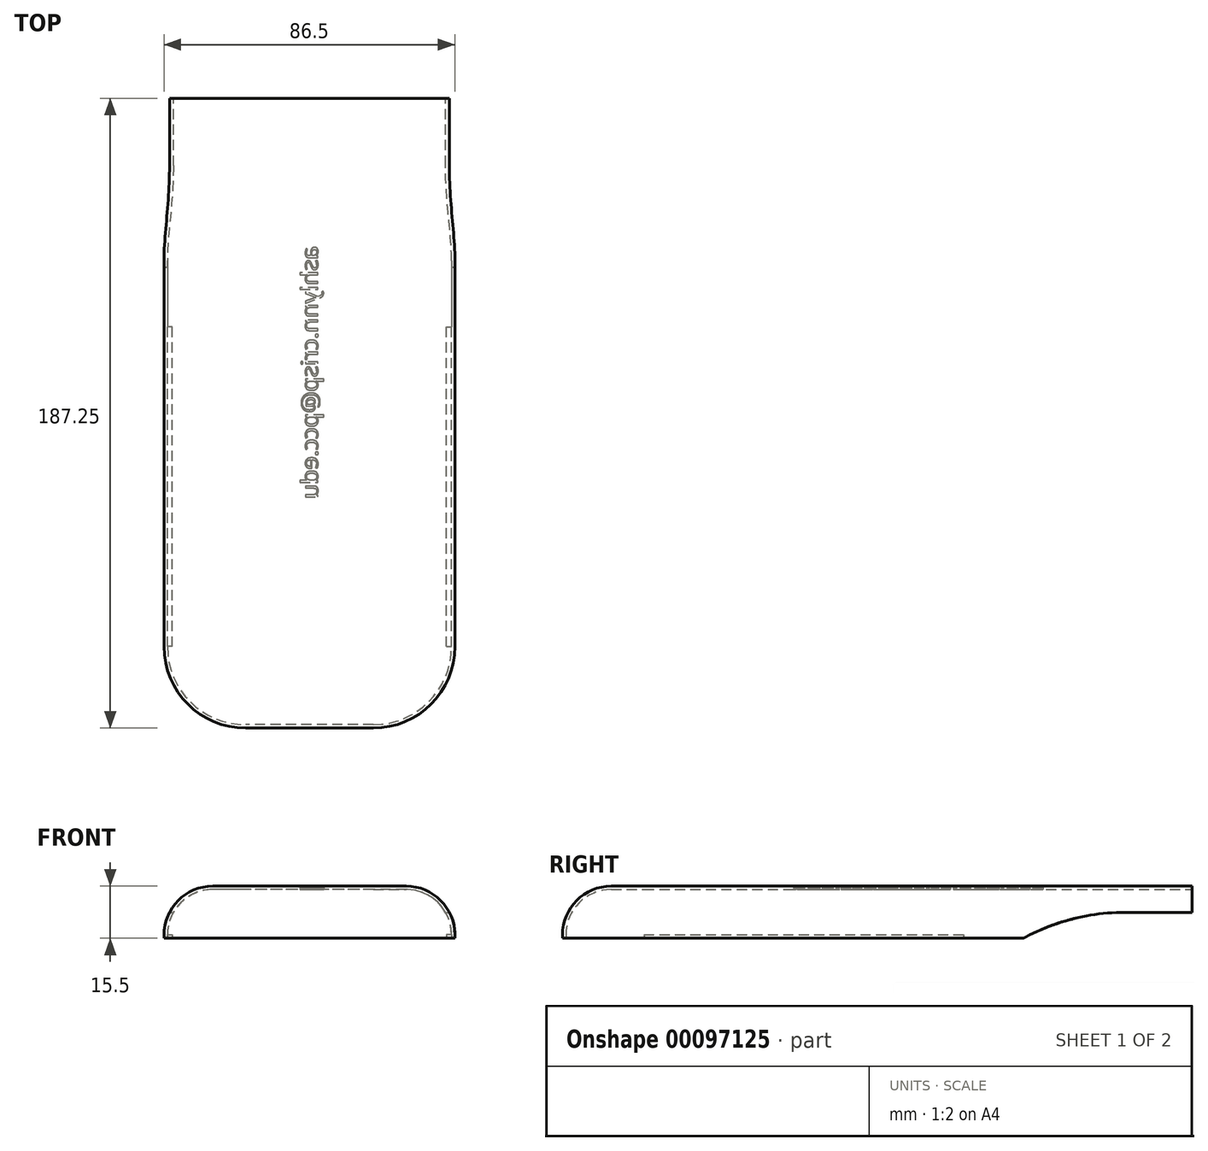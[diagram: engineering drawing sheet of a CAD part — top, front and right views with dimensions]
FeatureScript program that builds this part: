
annotation { "Feature Type Name" : "Feature", "Feature Type Description" : "" }
export const myFeature = defineFeature(function(context is Context, id is Id, definition is map)
    precondition{}
    {
        {
            var Q0;
            Q0=qCreatedBy(makeId("Front.planeOp"),FACE);
            var sketch = newSketch(context, id + "F0", { "sketchPlane" : qUnion([Q0])});
            skLineSegment(sketch, "E0", {"start": v(-28.75, 15.5) * mm, "end": v(0, 15.5) * mm});
            skLineSegment(sketch, "E1", {"start": v(0, 14.5) * mm, "end": v(-28.75, 14.5) * mm});
            skArc(sketch, "E2", {"start": v(-28.75, 15.5) * mm, "mid": v(-39, 11.25) * mm, "end": v(-43.25, 1) * mm});
            skArc(sketch, "E3", {"start": v(-28.75, 14.5) * mm, "mid": v(-38.3, 10.55) * mm, "end": v(-42.25, 1) * mm});
            skLineSegment(sketch, "E4", {"start": v(-43.25, 1) * mm, "end": v(-43.25, 0) * mm});
            skLineSegment(sketch, "E5", {"start": v(-43.25, 0) * mm, "end": v(-42.25, 0) * mm});
            skLineSegment(sketch, "E6", {"start": v(-42.25, 1) * mm, "end": v(-40.75, 1) * mm});
            skLineSegment(sketch, "E7", {"start": v(-40.75, 1) * mm, "end": v(-40.75, 0) * mm});
            skLineSegment(sketch, "E8", {"start": v(-40.75, 0) * mm, "end": v(-42.25, 0) * mm});
            skLineSegment(sketch, "E9", {"start": v(0, 15.5) * mm, "end": v(0, 14.5) * mm});
            skSolve(sketch);
        }
        {
            var Q0;
            Q0=makeQuery(id+"F0.imprint","IMPRINT",FACE,{"disambiguationData":[TD([[makeQuery(id+"F0.imprint","IMPRINT",EDGE,{"derivedFrom":sQuery(id+"F0.wireOp",EDGE,"E0")}),-1.0]])]});
            extrude(context, id + "F1", {"entities" : qUnion([Q0]), "depth" : 95 * mm});
        }
        {
            var Q0;
            Q0=makeQuery(id+"F1.opExtrude","CAP_FACE",FACE,{"disambiguationData":[OSD([sQuery(id+"F0.wireOp",EDGE,"E0"),sQuery(id+"F0.wireOp",EDGE,"E1"),sQuery(id+"F0.wireOp",EDGE,"E2"),sQuery(id+"F0.wireOp",EDGE,"E3"),sQuery(id+"F0.wireOp",EDGE,"E4"),sQuery(id+"F0.wireOp",EDGE,"E5"),sQuery(id+"F0.wireOp",EDGE,"E6"),sQuery(id+"F0.wireOp",EDGE,"E7"),sQuery(id+"F0.wireOp",EDGE,"E8"),sQuery(id+"F0.wireOp",EDGE,"a0cf0cd2-0adc-428c-8f04-1908610eca040.MirrorCS"),sQuery(id+"F0.wireOp",EDGE,"a0cf0cd2-0adc-428c-8f04-1908610eca042.MirrorCS"),sQuery(id+"F0.wireOp",EDGE,"a0cf0cd2-0adc-428c-8f04-1908610eca043.MirrorCS"),sQuery(id+"F0.wireOp",EDGE,"a0cf0cd2-0adc-428c-8f04-1908610eca044.MirrorCS"),sQuery(id+"F0.wireOp",EDGE,"a0cf0cd2-0adc-428c-8f04-1908610eca045.MirrorCS"),sQuery(id+"F0.wireOp",EDGE,"a0cf0cd2-0adc-428c-8f04-1908610eca046.MirrorCS"),sQuery(id+"F0.wireOp",EDGE,"a0cf0cd2-0adc-428c-8f04-1908610eca047.MirrorCS"),sQuery(id+"F0.wireOp",EDGE,"a0cf0cd2-0adc-428c-8f04-1908610eca048.MirrorCS"),sQuery(id+"F0.wireOp",EDGE,"e27b2194-398d-4e29-9fbd-8609b71e9a3b0.MirrorCS")])],"isStart":true});
            var sketch = newSketch(context, id + "F2", { "sketchPlane" : qUnion([Q0])});
            skLineSegment(sketch, "E10.MirrorCS", {"start": v(42.25, 1) * mm, "end": v(42.25, 0) * mm});
            skSolve(sketch);
        }
        {
            var Q0;
            {var subQ2=sQuery(id+"F2.wireOp",EDGE,"E10.MirrorCS");Q0=makeQuery(id+"F2.imprint","IMPRINT",FACE,{"disambiguationData":[TD([[makeQuery(id+"F2.imprint","IMPRINT",EDGE,{"derivedFrom":subQ2}),1.0]])]});}
            extrude(context, id + "F3", {"entities" : qUnion([Q0]), "operationType" : NewBodyOperationType.ADD, "depth" : 68 * mm});
        }
        {
            var Q0;
            Q0=makeQuery(id+"F1.opExtrude","CAP_FACE",FACE,{"disambiguationData":[OSD([sQuery(id+"F0.wireOp",EDGE,"E0"),sQuery(id+"F0.wireOp",EDGE,"E1"),sQuery(id+"F0.wireOp",EDGE,"E2"),sQuery(id+"F0.wireOp",EDGE,"E3"),sQuery(id+"F0.wireOp",EDGE,"E4"),sQuery(id+"F0.wireOp",EDGE,"E5"),sQuery(id+"F0.wireOp",EDGE,"E6"),sQuery(id+"F0.wireOp",EDGE,"E7"),sQuery(id+"F0.wireOp",EDGE,"E8"),sQuery(id+"F0.wireOp",EDGE,"a0cf0cd2-0adc-428c-8f04-1908610eca040.MirrorCS"),sQuery(id+"F0.wireOp",EDGE,"a0cf0cd2-0adc-428c-8f04-1908610eca042.MirrorCS"),sQuery(id+"F0.wireOp",EDGE,"a0cf0cd2-0adc-428c-8f04-1908610eca043.MirrorCS"),sQuery(id+"F0.wireOp",EDGE,"a0cf0cd2-0adc-428c-8f04-1908610eca044.MirrorCS"),sQuery(id+"F0.wireOp",EDGE,"a0cf0cd2-0adc-428c-8f04-1908610eca045.MirrorCS"),sQuery(id+"F0.wireOp",EDGE,"a0cf0cd2-0adc-428c-8f04-1908610eca046.MirrorCS"),sQuery(id+"F0.wireOp",EDGE,"a0cf0cd2-0adc-428c-8f04-1908610eca047.MirrorCS"),sQuery(id+"F0.wireOp",EDGE,"a0cf0cd2-0adc-428c-8f04-1908610eca048.MirrorCS"),sQuery(id+"F0.wireOp",EDGE,"e27b2194-398d-4e29-9fbd-8609b71e9a3b0.MirrorCS")])],"isStart":false});
            var sketch = newSketch(context, id + "F4", { "sketchPlane" : qUnion([Q0])});
            skLineSegment(sketch, "E11", {"start": v(-42.25, 1) * mm, "end": v(-42.25, 0) * mm});
            skLineSegment(sketch, "E12", {"start": v(-28.75, 15.5) * mm, "end": v(-28.75, 14.5) * mm});
            skLineSegment(sketch, "E13", {"start": v(-19, 15.5) * mm, "end": v(-19, 14.5) * mm});
            skSolve(sketch);
        }
        {
            var Q0;
            {var subQ0=sQuery(id+"F4.wireOp",EDGE,"E11");Q0=makeQuery(id+"F4.imprint","IMPRINT",FACE,{"disambiguationData":[TD([[makeQuery(id+"F4.imprint","IMPRINT",EDGE,{"derivedFrom":subQ0}),-1.0]])]});}
            var Q1;
            {var subQ0=sQuery(id+"F4.wireOp",EDGE,"E12");Q1=makeQuery(id+"F4.imprint","IMPRINT",FACE,{"disambiguationData":[TD([[makeQuery(id+"F4.imprint","IMPRINT",EDGE,{"derivedFrom":subQ0}),1.0]])]});}
            var Q2;
            Q2=sQuery(id+"F4.wireOp",EDGE,"E13");
            revolve(context, id + "F5", {"operationType" : NewBodyOperationType.ADD, "entities" : qUnion([Q0, Q1]), "axis" : qUnion([Q2]), "revolveType" : RevolveType.ONE_DIRECTION, "oppositeDirection" : true, "angle" : 90 * degree});
        }
        {
            var Q0;
            Q0=makeQuery(id+"F5.opRevolve","CAP_FACE",FACE,{"disambiguationData":[OSD([sQuery(id+"F0.wireOp",EDGE,"E0"),sQuery(id+"F0.wireOp",EDGE,"E1"),sQuery(id+"F0.wireOp",EDGE,"E2"),sQuery(id+"F0.wireOp",EDGE,"E3"),sQuery(id+"F0.wireOp",EDGE,"E4"),sQuery(id+"F0.wireOp",EDGE,"E5"),sQuery(id+"F0.wireOp",EDGE,"E8"),sQuery(id+"F4.wireOp",EDGE,"E11"),sQuery(id+"F4.wireOp",EDGE,"E13")])],"isStart":false});
            var sketch = newSketch(context, id + "F6", { "sketchPlane" : qUnion([Q0])});
            skLineSegment(sketch, "E14", {"start": v(-104.75, 15.5) * mm, "end": v(-104.75, 14.5) * mm});
            skSolve(sketch);
        }
        {
            var Q0;
            Q0=makeQuery(id+"F6.imprint","IMPRINT",FACE,{"disambiguationData":[TD([[makeQuery(id+"F6.imprint","IMPRINT",EDGE,{"derivedFrom":sQuery(id+"F6.wireOp",EDGE,"E14")}),1.0]])]});
            var Q1;
            {var subQ0=sQuery(id+"F0.wireOp",EDGE,"E9");Q1=makeQuery(id+"F3.boolean.opBoolean","MERGE",FACE,{"derivedFrom":[makeQuery(id+"F1.opExtrude","SWEPT_FACE",FACE,{"disambiguationData":[OSD([subQ0])]}),makeQuery(id+"F3.opExtrude","SWEPT_FACE",FACE,{"disambiguationData":[OSD([subQ0])]})]});}
            extrude(context, id + "F7", {"entities" : qUnion([Q0]), "operationType" : NewBodyOperationType.ADD, "endBound" : BoundingType.UP_TO_SURFACE, "endBoundEntityFace" : qUnion([Q1]), "depth" : 25 * mm});
        }
        {
            var Q0;
            Q0=makeQuery(id+"F5.opRevolve","CAP_FACE",FACE,{"disambiguationData":[OSD([sQuery(id+"F0.wireOp",EDGE,"E0"),sQuery(id+"F0.wireOp",EDGE,"E1"),sQuery(id+"F0.wireOp",EDGE,"E2"),sQuery(id+"F0.wireOp",EDGE,"E3"),sQuery(id+"F0.wireOp",EDGE,"E4"),sQuery(id+"F0.wireOp",EDGE,"E5"),sQuery(id+"F0.wireOp",EDGE,"E8"),sQuery(id+"F4.wireOp",EDGE,"E11"),sQuery(id+"F4.wireOp",EDGE,"E13")])],"isStart":false});
            var Q1;
            {var subQ0=sQuery(id+"F0.wireOp",EDGE,"E9");Q1=makeQuery(id+"F7.boolean.opBoolean","MERGE",FACE,{"derivedFrom":[makeQuery(id+"F3.boolean.opBoolean","MERGE",FACE,{"derivedFrom":[makeQuery(id+"F1.opExtrude","SWEPT_FACE",FACE,{"disambiguationData":[OSD([subQ0])]}),makeQuery(id+"F3.opExtrude","SWEPT_FACE",FACE,{"disambiguationData":[OSD([subQ0])]})]}),makeQuery(id+"F7.opExtrude","CAP_FACE",FACE,{"disambiguationData":[OSD([subQ0])],"isStart":false})]});}
            extrude(context, id + "F8", {"entities" : qUnion([Q0]), "operationType" : NewBodyOperationType.ADD, "endBound" : BoundingType.UP_TO_SURFACE, "endBoundEntityFace" : qUnion([Q1]), "depth" : 25 * mm});
        }
        {
            var Q0;
            Q0=makeQuery(id+"F1.opExtrude","SWEPT_BODY",BODY,{"disambiguationData":[OSD([sQuery(id+"F0.wireOp",EDGE,"E0"),sQuery(id+"F0.wireOp",EDGE,"E1"),sQuery(id+"F0.wireOp",EDGE,"E2"),sQuery(id+"F0.wireOp",EDGE,"E3"),sQuery(id+"F0.wireOp",EDGE,"E4"),sQuery(id+"F0.wireOp",EDGE,"E5"),sQuery(id+"F0.wireOp",EDGE,"E6"),sQuery(id+"F0.wireOp",EDGE,"E7"),sQuery(id+"F0.wireOp",EDGE,"E8"),sQuery(id+"F0.wireOp",EDGE,"E9")])]});
            var Q1;
            Q1=qCreatedBy(makeId("Right.planeOp"),FACE);
            mirror(context, id + "F9", {"operationType" : NewBodyOperationType.ADD, "entities" : qUnion([Q0]), "mirrorPlane" : qUnion([Q1])});
        }
        {
            var Q0;
            {var subQ0=sQuery(id+"F0.wireOp",EDGE,"E4");var subQ1=sQuery(id+"F0.wireOp",EDGE,"E2");Q0=makeQuery(id+"FFDJrICMNDunt1b_1.splitOp","SPLIT",EDGE,{"derivedFrom":makeQuery(id+"F9.opPattern","COPY",EDGE,{"derivedFrom":makeQuery(id+"F3.boolean.opBoolean","MERGE",EDGE,{"derivedFrom":[makeQuery(id+"F1.opExtrude","SWEPT_EDGE",EDGE,{"disambiguationData":[OSD([subQ1,subQ0])]}),makeQuery(id+"F3.opExtrude","SWEPT_EDGE",EDGE,{"disambiguationData":[OSD([subQ1,subQ0])]})]}),"instanceName":"1"}),"isFromBackBody":true});}
            cPlane(context, id + "F10", {"entities" : qUnion([Q0]), "cplaneType" : CPlaneType.LINE_ANGLE, "offset" : 25 * mm, "angle" : 90 * degree, "width" : 150 * mm, "height" : 150 * mm});
        }
        {
            var Q0;
            Q0=qCreatedBy(id+"F10.planeOp",FACE);
            var sketch = newSketch(context, id + "F11", { "sketchPlane" : qUnion([Q0])});
            skLineSegment(sketch, "E15.0", {"start": v(-95, 0) * mm, "end": v(68, 0) * mm});
            skLineSegment(sketch, "E16.0", {"start": v(68, 15.5) * mm, "end": v(68, 1) * mm});
            skLineSegment(sketch, "E17.0", {"start": v(68, 1) * mm, "end": v(68, 0) * mm});
            skArc(sketch, "E18", {"start": v(48, 7.7) * mm, "mid": v(32.43, 5.74) * mm, "end": v(17.82, 0) * mm});
            skLineSegment(sketch, "E19", {"start": v(48, 7.7) * mm, "end": v(68, 7.7) * mm});
            skSolve(sketch);
        }
        {
            var Q0;
            {var subQ1=sQuery(id+"F11.wireOp",EDGE,"E17.0");Q0=makeQuery(id+"F11.imprint","IMPRINT",FACE,{"disambiguationData":[TD([[makeQuery(id+"F11.imprint","IMPRINT",EDGE,{"derivedFrom":subQ1}),-1.0]])]});}
            var Q1;
            {var subQ0=sQuery(id+"F0.wireOp",EDGE,"E4");Q1=makeQuery(id+"F3.boolean.opBoolean","MERGE",FACE,{"derivedFrom":[makeQuery(id+"F1.opExtrude","SWEPT_FACE",FACE,{"disambiguationData":[OSD([subQ0])]}),makeQuery(id+"F3.opExtrude","SWEPT_FACE",FACE,{"disambiguationData":[OSD([subQ0])]})]});}
            extrude(context, id + "F12", {"entities" : qUnion([Q0]), "operationType" : NewBodyOperationType.REMOVE, "endBound" : BoundingType.UP_TO_SURFACE, "oppositeDirection" : true, "endBoundEntityFace" : qUnion([Q1]), "depth" : 25 * mm});
        }
        {
            var Q0;
            Q0=makeQuery(id+"FFDJrICMNDunt1b_1.splitOp","SPLIT",BODY,{"derivedFrom":makeQuery(id+"F1.opExtrude","SWEPT_BODY",BODY,{"disambiguationData":[OSD([sQuery(id+"F0.wireOp",EDGE,"E0"),sQuery(id+"F0.wireOp",EDGE,"E1"),sQuery(id+"F0.wireOp",EDGE,"E2"),sQuery(id+"F0.wireOp",EDGE,"E3"),sQuery(id+"F0.wireOp",EDGE,"E4"),sQuery(id+"F0.wireOp",EDGE,"E5"),sQuery(id+"F0.wireOp",EDGE,"E6"),sQuery(id+"F0.wireOp",EDGE,"E7"),sQuery(id+"F0.wireOp",EDGE,"E8"),sQuery(id+"F0.wireOp",EDGE,"E9")])]})});
            transform(context, id + "F13", {"entities" : qUnion([Q0]), "transformType" : TransformType.TRANSLATION_3D, "dx" : 180 * mm, "dy" : 0 * mm, "dz" : 0 * mm, "makeCopy" : true});
        }
        {
            var Q0;
            Q0=makeQuery(id+"FVeOS4f5wFWiGPo_1.splitOp","SPLIT",BODY,{"derivedFrom":makeQuery(id+"F13.opPattern","COPY",BODY,{"derivedFrom":makeQuery(id+"FFDJrICMNDunt1b_1.splitOp","SPLIT",BODY,{"derivedFrom":makeQuery(id+"F1.opExtrude","SWEPT_BODY",BODY,{"disambiguationData":[OSD([sQuery(id+"F0.wireOp",EDGE,"E0"),sQuery(id+"F0.wireOp",EDGE,"E1"),sQuery(id+"F0.wireOp",EDGE,"E2"),sQuery(id+"F0.wireOp",EDGE,"E3"),sQuery(id+"F0.wireOp",EDGE,"E4"),sQuery(id+"F0.wireOp",EDGE,"E5"),sQuery(id+"F0.wireOp",EDGE,"E6"),sQuery(id+"F0.wireOp",EDGE,"E7"),sQuery(id+"F0.wireOp",EDGE,"E8"),sQuery(id+"F0.wireOp",EDGE,"E9")])]})}),"instanceName":"1"}),"isFromBackBody":true});
            deleteBodies(context, id + "F14", {"entities" : qUnion([Q0])});
        }
        {
            var Q0;
            {var subQ0=sQuery(id+"F0.wireOp",EDGE,"E1");var subQ1=makeQuery(id+"F7.boolean.opBoolean","MERGE",FACE,{"derivedFrom":[makeQuery(id+"F5.boolean.opBoolean","MERGE",FACE,{"derivedFrom":[makeQuery(id+"F3.boolean.opBoolean","MERGE",FACE,{"derivedFrom":[makeQuery(id+"F1.opExtrude","SWEPT_FACE",FACE,{"disambiguationData":[OSD([subQ0])]}),makeQuery(id+"F3.opExtrude","SWEPT_FACE",FACE,{"disambiguationData":[OSD([subQ0])]})]}),makeQuery(id+"F5.opRevolve","SWEPT_FACE",FACE,{"disambiguationData":[OSD([subQ0])]})]}),makeQuery(id+"F7.opExtrude","SWEPT_FACE",FACE,{"disambiguationData":[OSD([subQ0])]})]});Q0=makeQuery(id+"FFDJrICMNDunt1b_1.splitOp","SPLIT",FACE,{"derivedFrom":makeQuery(id+"F9.boolean.opBoolean","MERGE",FACE,{"derivedFrom":[subQ1,makeQuery(id+"F9.opPattern","COPY",FACE,{"derivedFrom":subQ1,"instanceName":"1"})]}),"isFromBackBody":true});}
            var sketch = newSketch(context, id + "F15", { "sketchPlane" : qUnion([Q0])});
            skText(sketch, "E20", { "text": "<email>", "fontName": "OpenSans-Regular.ttf"});
            skPoint(sketch, "E21", {"position": v(2.12, 43.7) * mm});
            skPoint(sketch, "E22", {"position": v(-28.75, 13.5) * mm});
            skPoint(sketch, "E23", {"position": v(0, 51) * mm});
            skPoint(sketch, "E24", {"position": v(0, 104.75) * mm});
            const initialGuessF15  = {"E20": [0.00254, -0.024, 0, 1, 0.00508]};
            skSetInitialGuess(sketch, initialGuessF15);
            skSolve(sketch);
        }
        {
            var Q0;
            Q0 = qSketchRegion(id + "F15", true);
            extrude(context, id + "F16", {"entities" : qUnion([Q0]), "operationType" : NewBodyOperationType.REMOVE, "oppositeDirection" : true, "depth" : 0.5 * mm});
        }
    });
